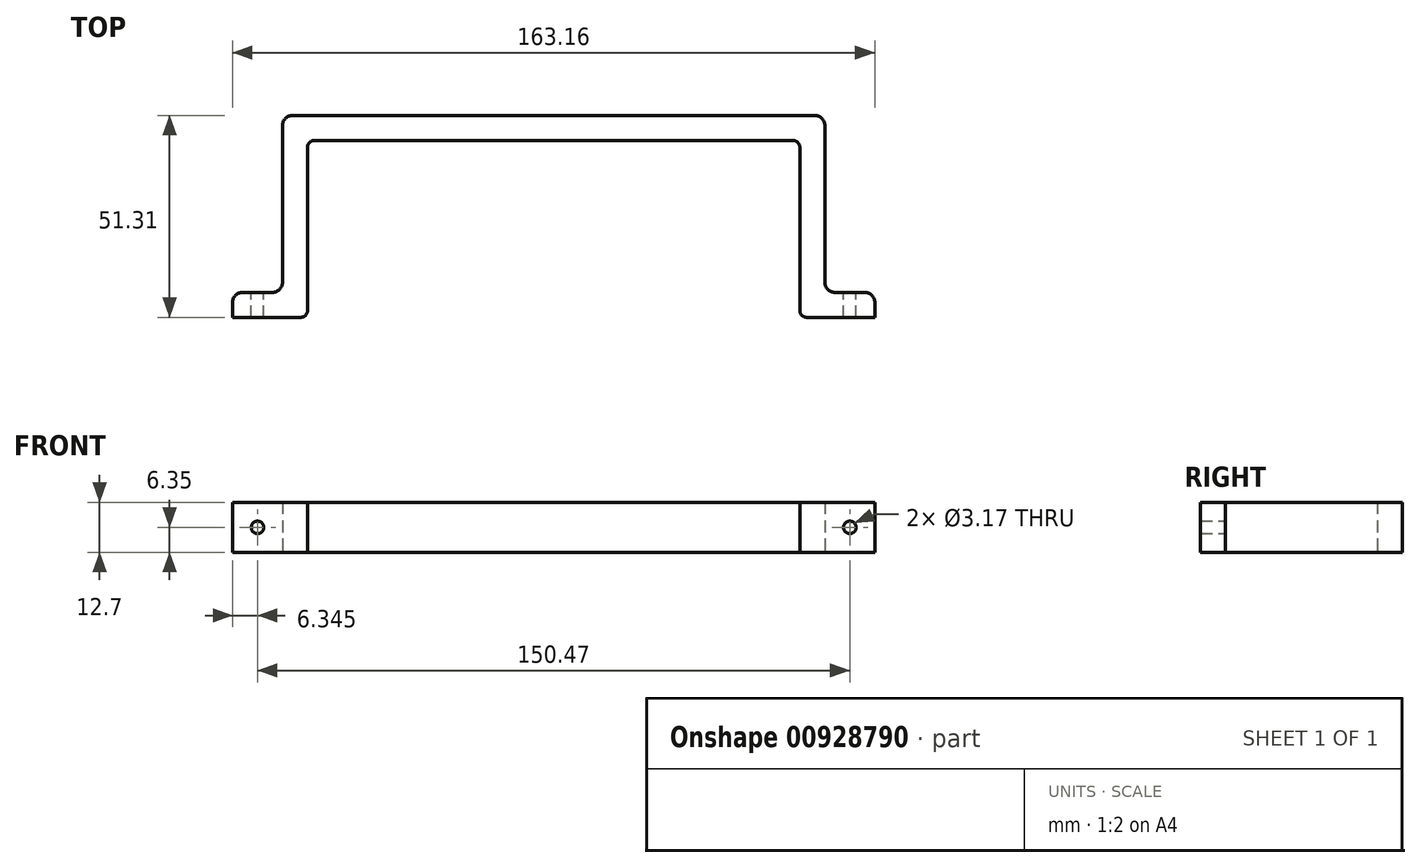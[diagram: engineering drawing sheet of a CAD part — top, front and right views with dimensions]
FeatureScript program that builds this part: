
annotation { "Feature Type Name" : "Feature", "Feature Type Description" : "" }
export const myFeature = defineFeature(function(context is Context, id is Id, definition is map)
    precondition{}
    {
        {
            var Q0;
            Q0=qCreatedBy(makeId("Top.planeOp"),FACE);
            var sketch = newSketch(context, id + "F0", { "sketchPlane" : qUnion([Q0])});
            skLineSegment(sketch, "E0", {"start": v(0, 0) * mm, "end": v(-62.53, 0) * mm});
            skLineSegment(sketch, "E1", {"start": v(-62.53, 0) * mm, "end": v(-62.53, -44.96) * mm});
            skLineSegment(sketch, "E2", {"start": v(-62.53, -44.96) * mm, "end": v(-81.58, -44.96) * mm});
            skLineSegment(sketch, "E3", {"start": v(-81.58, -44.96) * mm, "end": v(-81.58, -38.6) * mm});
            skLineSegment(sketch, "E4", {"start": v(-81.58, -38.6) * mm, "end": v(-68.88, -38.6) * mm});
            skLineSegment(sketch, "E5", {"start": v(-68.88, -38.6) * mm, "end": v(-68.88, 0) * mm});
            skLineSegment(sketch, "E6", {"start": v(-68.88, 0) * mm, "end": v(-68.88, 6.35) * mm});
            skLineSegment(sketch, "E7", {"start": v(-68.88, 6.35) * mm, "end": v(0, 6.35) * mm});
            skLineSegment(sketch, "E8.MirrorCS", {"start": v(81.58, -44.96) * mm, "end": v(81.58, -38.6) * mm});
            skLineSegment(sketch, "E9.MirrorCS", {"start": v(68.88, 0) * mm, "end": v(68.88, 6.35) * mm});
            skLineSegment(sketch, "E10.MirrorCS", {"start": v(0, 0) * mm, "end": v(62.53, 0) * mm});
            skLineSegment(sketch, "E11.MirrorCS", {"start": v(68.88, 6.35) * mm, "end": v(0, 6.35) * mm});
            skLineSegment(sketch, "E12.MirrorCS", {"start": v(81.58, -38.6) * mm, "end": v(68.88, -38.6) * mm});
            skLineSegment(sketch, "E13.MirrorCS", {"start": v(62.53, -44.96) * mm, "end": v(81.58, -44.96) * mm});
            skLineSegment(sketch, "E14.MirrorCS", {"start": v(62.53, 0) * mm, "end": v(62.53, -44.96) * mm});
            skLineSegment(sketch, "E15.MirrorCS", {"start": v(68.88, -38.6) * mm, "end": v(68.88, 0) * mm});
            skSolve(sketch);
        }
        {
            var Q0;
            Q0=makeQuery(id+"F0.imprint","IMPRINT",FACE,{"disambiguationData":[TD([[makeQuery(id+"F0.imprint","IMPRINT",EDGE,{"derivedFrom":sQuery(id+"F0.wireOp",EDGE,"E0")}),-1.0]])]});
            extrude(context, id + "F1", {"entities" : qUnion([Q0]), "depth" : 12.7 * mm, "offsetDistance" : 25.4 * mm});
        }
        {
            var Q0;
            Q0=makeQuery(id+"F1.opExtrude","SWEPT_FACE",FACE,{"disambiguationData":[OSD([sQuery(id+"F0.wireOp",EDGE,"E4")])]});
            var sketch = newSketch(context, id + "F2", { "sketchPlane" : qUnion([Q0])});
            skCircle(sketch, "E16", {"center": v(-75.23, 6.35) * mm, "radius": 1.59 * mm});
            skSolve(sketch);
        }
        {
            var Q0;
            {var subQ0=sQuery(id+"F0.wireOp",EDGE,"E4");Q0=makeQuery(id+"F2.imprint","IMPRINT",FACE,{"disambiguationData":[TD([[makeQuery(id+"F2.imprint","IMPRINT",EDGE,{"derivedFrom":makeQuery(id+"F1.opExtrude","CAP_EDGE",EDGE,{"disambiguationData":[OSD([subQ0])],"isStart":true})}),-1.0]])]});}
            var sketch = newSketch(context, id + "F3", { "sketchPlane" : qUnion([Q0])});
            skPoint(sketch, "E17.0", {"position": v(68.88, 6.35) * mm});
            skPoint(sketch, "E18.0", {"position": v(75.23, 12.7) * mm});
            skPoint(sketch, "E19.0", {"position": v(81.58, 6.35) * mm});
            skPoint(sketch, "E20.0", {"position": v(75.23, 0) * mm});
            skCircle(sketch, "E21", {"center": v(75.23, 6.35) * mm, "radius": 1.59 * mm});
            skSolve(sketch);
        }
        {
            var Q0;
            Q0=makeQuery(id+"F3.imprint","IMPRINT",FACE,{"disambiguationData":[TD([[makeQuery(id+"F3.imprint","IMPRINT",EDGE,{"derivedFrom":sQuery(id+"F3.wireOp",EDGE,"E21")}),1.0]])]});
            var Q1;
            Q1=sQuery(id+"F3.wireOp",EDGE,"E21");
            extrude(context, id + "F4", {"entities" : qUnion([Q0]), "operationType" : NewBodyOperationType.REMOVE, "surfaceEntities" : qUnion([Q1]), "oppositeDirection" : true, "depth" : 25.4 * mm, "offsetDistance" : 25.4 * mm});
        }
        {
            var Q0;
            Q0=makeQuery(id+"F2.imprint","IMPRINT",FACE,{"disambiguationData":[TD([[makeQuery(id+"F2.imprint","IMPRINT",EDGE,{"derivedFrom":sQuery(id+"F2.wireOp",EDGE,"E16")}),1.0]])]});
            extrude(context, id + "F5", {"entities" : qUnion([Q0]), "operationType" : NewBodyOperationType.REMOVE, "oppositeDirection" : true, "depth" : 25.4 * mm, "offsetDistance" : 25.4 * mm});
        }
        {
            var Q0;
            Q0=makeQuery(id+"F1.opExtrude","SWEPT_EDGE",EDGE,{"disambiguationData":[OSD([sQuery(id+"F0.wireOp",EDGE,"E8.MirrorCS"),sQuery(id+"F0.wireOp",EDGE,"E12.MirrorCS")])]});
            var Q1;
            Q1=makeQuery(id+"F1.opExtrude","SWEPT_EDGE",EDGE,{"disambiguationData":[OSD([sQuery(id+"F0.wireOp",EDGE,"E9.MirrorCS"),sQuery(id+"F0.wireOp",EDGE,"E11.MirrorCS")])]});
            var Q2;
            Q2=makeQuery(id+"F1.opExtrude","SWEPT_EDGE",EDGE,{"disambiguationData":[OSD([sQuery(id+"F0.wireOp",EDGE,"E12.MirrorCS"),sQuery(id+"F0.wireOp",EDGE,"E15.MirrorCS")])]});
            var Q3;
            Q3=makeQuery(id+"F1.opExtrude","SWEPT_EDGE",EDGE,{"disambiguationData":[OSD([sQuery(id+"F0.wireOp",EDGE,"E6"),sQuery(id+"F0.wireOp",EDGE,"E7")])]});
            var Q4;
            Q4=makeQuery(id+"F1.opExtrude","SWEPT_EDGE",EDGE,{"disambiguationData":[OSD([sQuery(id+"F0.wireOp",EDGE,"E4"),sQuery(id+"F0.wireOp",EDGE,"E5")])]});
            var Q5;
            Q5=makeQuery(id+"F1.opExtrude","SWEPT_EDGE",EDGE,{"disambiguationData":[OSD([sQuery(id+"F0.wireOp",EDGE,"E3"),sQuery(id+"F0.wireOp",EDGE,"E4")])]});
            fillet(context, id + "F6", {"entities" : qUnion([Q0, Q1, Q2, Q3, Q4, Q5]), "radius" : 2.54 * mm, "tangentPropagation" : true, "allowEdgeOverflow" : false});
        }
        {
            var Q0;
            Q0=makeQuery(id+"F1.opExtrude","SWEPT_EDGE",EDGE,{"disambiguationData":[OSD([sQuery(id+"F0.wireOp",EDGE,"E10.MirrorCS"),sQuery(id+"F0.wireOp",EDGE,"E14.MirrorCS")])]});
            var Q1;
            Q1=makeQuery(id+"F1.opExtrude","SWEPT_EDGE",EDGE,{"disambiguationData":[OSD([sQuery(id+"F0.wireOp",EDGE,"E0"),sQuery(id+"F0.wireOp",EDGE,"E1")])]});
            var Q2;
            Q2=makeQuery(id+"F1.opExtrude","SWEPT_EDGE",EDGE,{"disambiguationData":[OSD([sQuery(id+"F0.wireOp",EDGE,"E1"),sQuery(id+"F0.wireOp",EDGE,"E2")])]});
            var Q3;
            Q3=makeQuery(id+"F1.opExtrude","SWEPT_EDGE",EDGE,{"disambiguationData":[OSD([sQuery(id+"F0.wireOp",EDGE,"E13.MirrorCS"),sQuery(id+"F0.wireOp",EDGE,"E14.MirrorCS")])]});
            fillet(context, id + "F7", {"entities" : qUnion([Q0, Q1, Q2, Q3]), "radius" : 1.78 * mm, "tangentPropagation" : true, "allowEdgeOverflow" : false});
        }
    });
